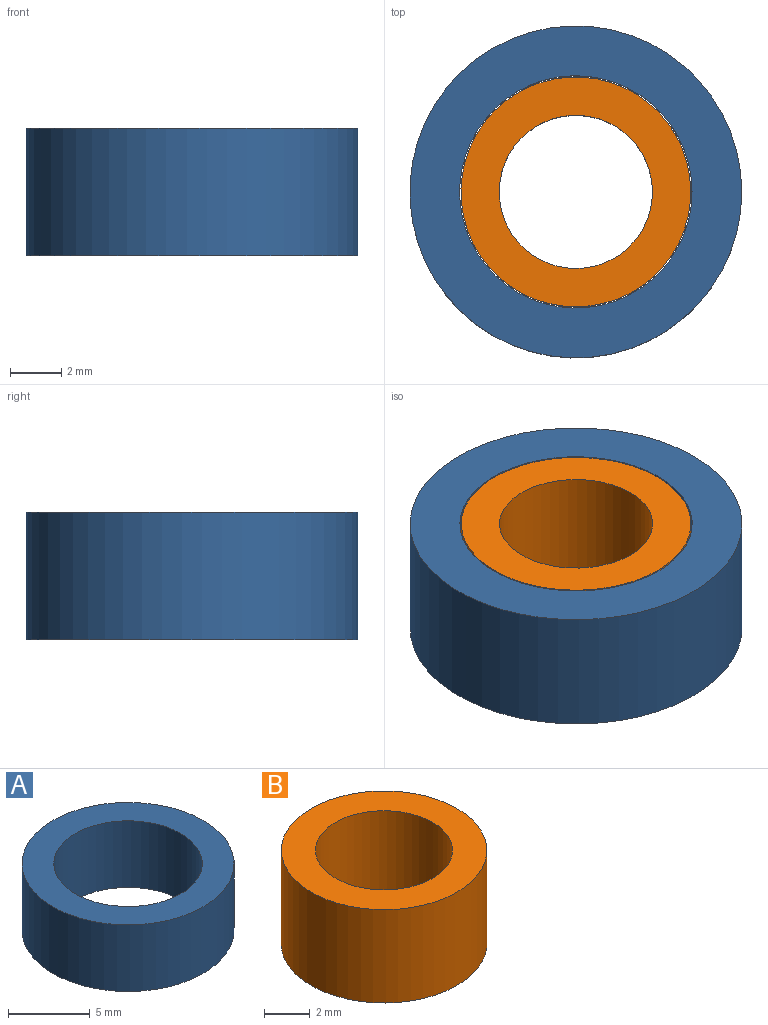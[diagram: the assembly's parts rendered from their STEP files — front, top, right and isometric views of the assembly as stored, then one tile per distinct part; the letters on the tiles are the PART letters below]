
ASSEMBLY  parts=2 mates=1
PART A: 4 faces, bbox 13x13x5 mm
  f0: cylinder r=4.55mm len=9.1mm, axis (0,0,-1), area 142.9mm2, adj f2,f3
  f1: cylinder r=6.5mm len=13mm, axis (0,0,-1), area 204.2mm2, adj f2,f3
  f2: plane 13x13mm, normal (0,0,1), area 67.7mm2, adj f0,f1
  f3: plane 13x13mm, normal (0,0,-1), area 67.7mm2, adj f0,f1
PART B: 4 faces, bbox 9x9x5 mm
  f0: cylinder r=3mm len=6mm, axis (0,0,-1), area 94.2mm2, adj f2,f3
  f1: cylinder r=4.5mm len=9mm, axis (0,0,-1), area 141.4mm2, adj f2,f3
  f2: plane 9x9mm, normal (0,0,1), area 35.3mm2, adj f0,f1
  f3: plane 9x9mm, normal (0,0,-1), area 35.3mm2, adj f0,f1
PLACE A t=(-3.08,-0.45,-0.5)mm
PLACE B rot(axis=(0,0,1),150deg) t=(-3.08,-0.45,-0.5)mm
MATE revolute B.f0 <-> A.f0  axis (0,0,-1) through (-3.08,-0.45,4.5)mm
